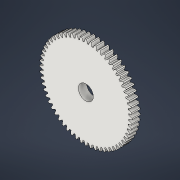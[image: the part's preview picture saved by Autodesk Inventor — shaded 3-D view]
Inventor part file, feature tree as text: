
AUTODESK INVENTOR PART (.ipt)
format: ipt  version: 2021 (Build 250183000, 183)  size: 391,680 bytes
history: native  units: mm (DEFAULTED — no unit token found)
features: plane x3, other x3, sketch x3, extrude x2
ambient origin geometry x8: Origin, YZ Plane, XZ Plane, XY Plane, X Axis, Y Axis, Z Axis, Center Point
bodies: Solid1 (feature_tree)
feature tree (11):
  extrude  "Extrusion1"  Depth=0.5mm TaperAngle=0.0deg
  plane  "Work Plane2"
  plane  "Work Plane8"
  plane  "Work Plane9"
  other  "Engrenagem reta"
  extrude  "Extrusão2"  Depth=10.0mm TaperAngle=0.0deg
  sketch  "Sketch1"  dims[d0=5.575177mm d1=0.5mm d2=0.0mm]
  sketch  "Sketch2"  dims[d3=5.4mm d4=10.0mm d5=0.0mm]
  other  "Srf1"
  sketch  "Esboço3"  dims[d16=3.597588mm d17=0.0mm d34=0.523599mm d39=0.0mm d41=0.0mm d43=3.597588mm d46=3.597588mm d47=0.0mm d48=0.0mm d49=0.9mm d50=0.5mm d51=0.0mm]
  other  "Diâmetro do flanco"
